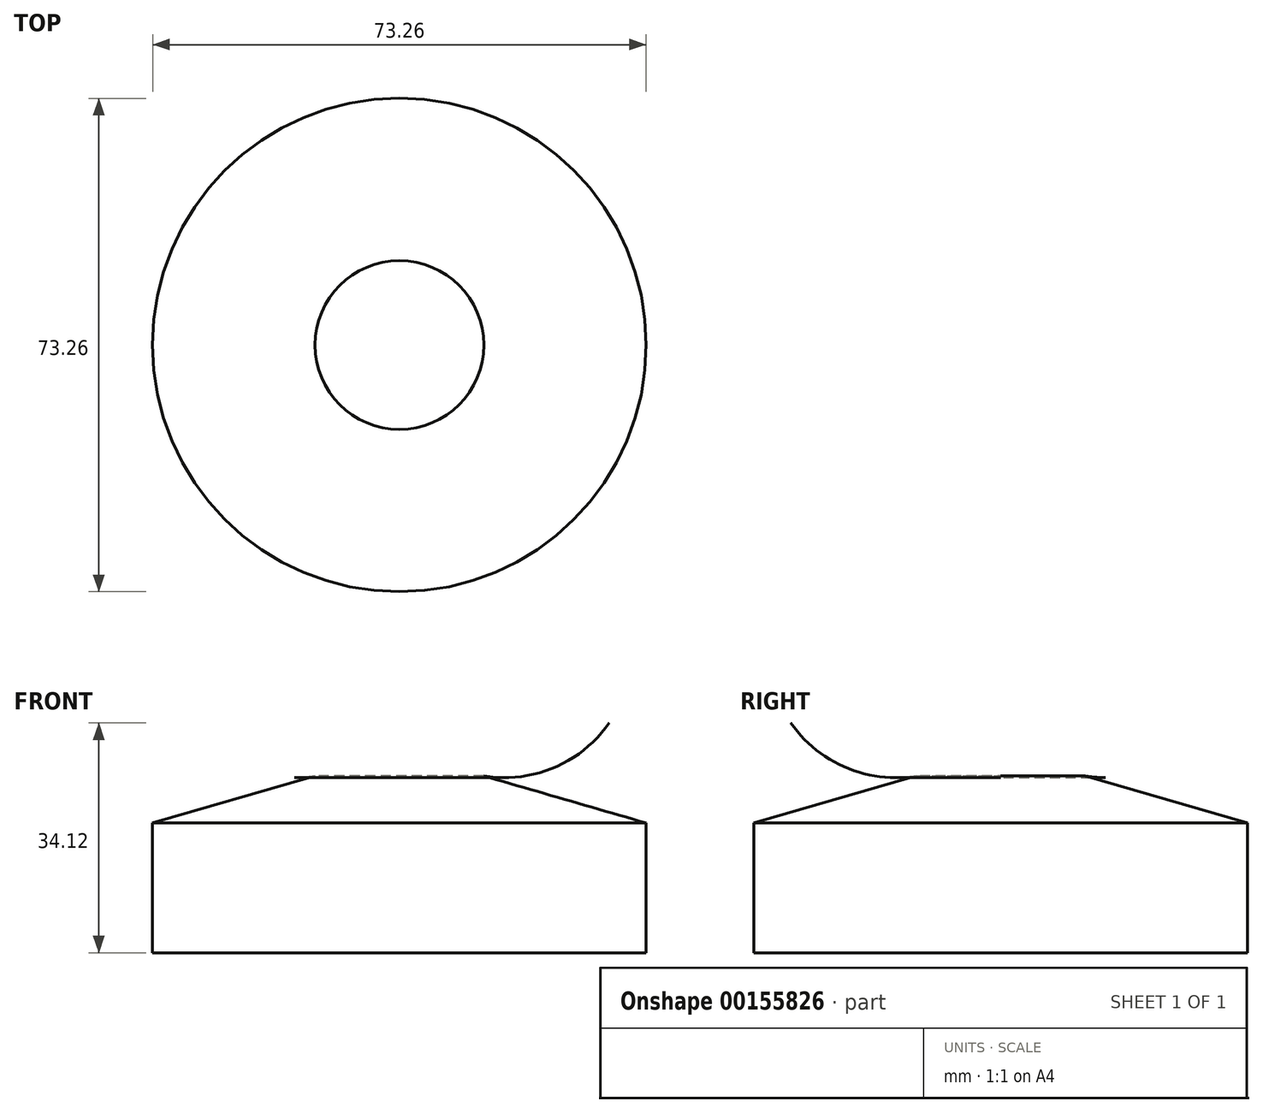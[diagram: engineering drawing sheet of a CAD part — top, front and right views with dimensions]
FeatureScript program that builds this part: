
annotation { "Feature Type Name" : "Feature", "Feature Type Description" : "" }
export const myFeature = defineFeature(function(context is Context, id is Id, definition is map)
    precondition{}
    {
        {
            var Q0;
            Q0=qCreatedBy(makeId("Front.planeOp"),FACE);
            var sketch = newSketch(context, id + "F0", { "sketchPlane" : qUnion([Q0])});
            skLineSegment(sketch, "E0", {"start": v(0, 0) * mm, "end": v(36.63, 0) * mm});
            skLineSegment(sketch, "E1", {"start": v(36.63, 0) * mm, "end": v(36.63, 19.27) * mm});
            skLineSegment(sketch, "E2", {"start": v(36.63, 19.27) * mm, "end": v(12.53, 26.25) * mm});
            skArc(sketch, "E3", {"start": v(12.53, 26.25) * mm, "mid": v(33.1, 52.4) * mm, "end": v(0, 55.9) * mm});
            skLineSegment(sketch, "E4", {"start": v(0, 55.9) * mm, "end": v(0, 0) * mm});
            skSolve(sketch);
        }
        {
            var Q0;
            Q0=makeQuery(id+"F0.imprint","IMPRINT",FACE,{"disambiguationData":[TD([[makeQuery(id+"F0.imprint","IMPRINT",EDGE,{"derivedFrom":sQuery(id+"F0.wireOp",EDGE,"E0")}),1.0]])]});
            var Q1;
            Q1=sQuery(id+"F0.wireOp",EDGE,"E4");
            revolve(context, id + "F1", {"entities" : qUnion([Q0]), "axis" : qUnion([Q1]), "revolveType" : RevolveType.FULL});
        }
    });
